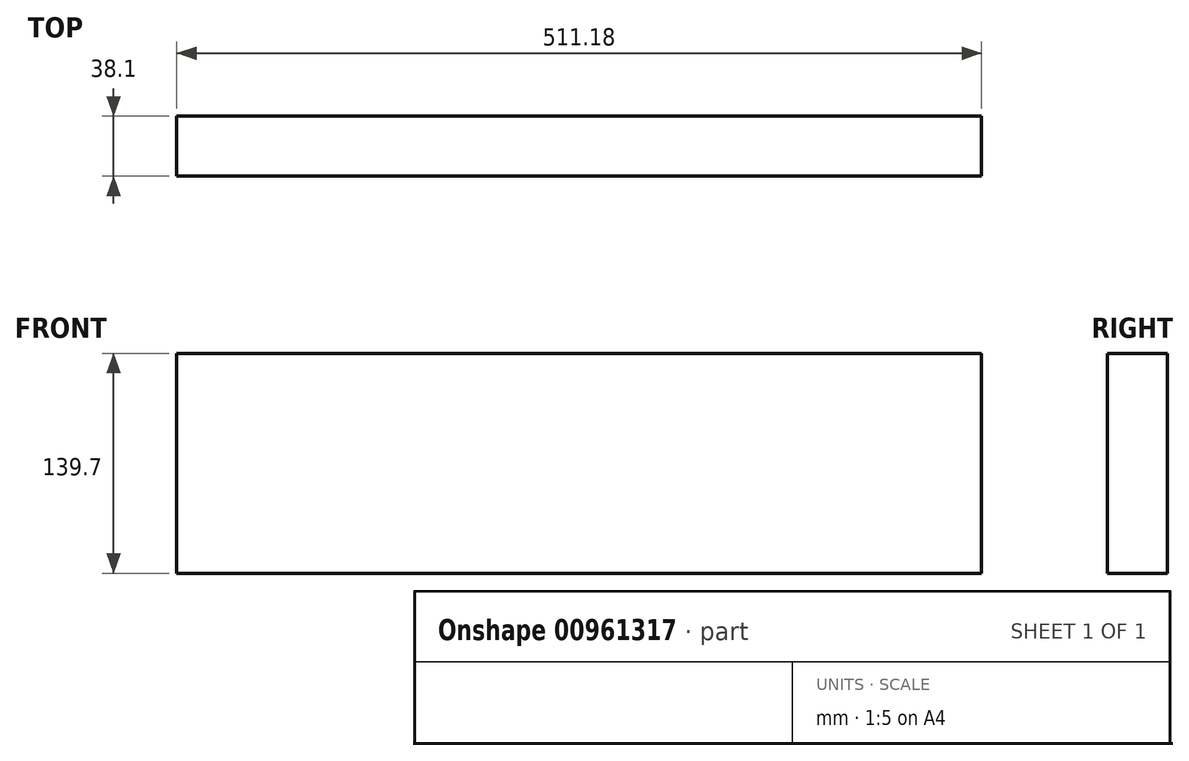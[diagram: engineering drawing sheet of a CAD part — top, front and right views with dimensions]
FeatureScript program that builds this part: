
annotation { "Feature Type Name" : "Feature", "Feature Type Description" : "" }
export const myFeature = defineFeature(function(context is Context, id is Id, definition is map)
    precondition{}
    {
        {
            var Q0;
            Q0=qCreatedBy(makeId("Right.planeOp"),FACE);
            var sketch = newSketch(context, id + "F0", { "sketchPlane" : qUnion([Q0])});
            skLineSegment(sketch, "E0.bottom", {"start": v(19.05, 69.85) * mm, "end": v(-19.05, 69.85) * mm});
            skLineSegment(sketch, "E0.top", {"start": v(19.05, -69.85) * mm, "end": v(-19.05, -69.85) * mm});
            skLineSegment(sketch, "E0.left", {"start": v(19.05, 69.85) * mm, "end": v(19.05, -69.85) * mm});
            skLineSegment(sketch, "E0.right", {"start": v(-19.05, 69.85) * mm, "end": v(-19.05, -69.85) * mm});
            skPoint(sketch, "E0.middle", {"position": v(0, 0) * mm});
            skSolve(sketch);
        }
        {
            var Q0;
            Q0=makeQuery(id+"F0.imprint","IMPRINT",FACE,{"disambiguationData":[TD([[makeQuery(id+"F0.imprint","IMPRINT",EDGE,{"derivedFrom":sQuery(id+"F0.wireOp",EDGE,"E0.bottom")}),1.0]])]});
            extrude(context, id + "F1", {"entities" : qUnion([Q0]), "endBound" : BoundingType.SYMMETRIC, "depth" : 511.17 * mm, "offsetDistance" : 25.4 * mm});
        }
    });
